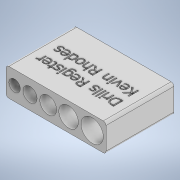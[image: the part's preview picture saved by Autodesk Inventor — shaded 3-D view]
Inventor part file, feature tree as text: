
AUTODESK INVENTOR PART (.ipt)
format: ipt  version: 2022.2 (Build 262287030, 287C)  size: 797,696 bytes
history: native  units: in
note: dims shown in document units (in); Inventor stores cm internally (conversion verified against a paired STEP export)
features: sketch x3, extrude x2, fillet x1, emboss x1
ambient origin geometry x8: Origin, YZ Plane, XZ Plane, XY Plane, X Axis, Y Axis, Z Axis, Center Point
bodies: Solid1 (feature_tree)
feature tree (7):
  extrude  "Extrusion1"  Depth=0.9in
  extrude  "Extrusion2"  Depth=0.775in
  fillet  "Fillet1"  Radius=0.101in
  emboss  "Emboss1"
  sketch  "Sketch1"  dims[d0=1.025in d1=0.9in]
  sketch  "Sketch2"  dims[d2=0.125in d3=0.775in d4=0.101in]
  sketch  "Sketch3"  dims[d5=0.125in d6=0.65in d7=0.125in d8=0.525in d9=0.125in d10=0.125in d11=0.125in d12=0.125in d13=3.0in d14=0.0in d15=0.125in d16=0.0in d17=0.125in d18=0.075in d19=0.0in]
